# Revit family: Weitspannkabelleiter - WKL 2040_2050_2060 FT
name_source: partatom
category: Generic Models
revit_build: Autodesk Revit 2017 (Build: 20190508_0315(x64)
units: mm (PartAtom-declared; Revit-internal decimal feet)

## family parameters
Always vertical = Yes
Can host rebar = No
Cut with Voids When Loaded = No
Part Type = Normal
Room Calculation Point = No
Round Connector Dimension = Use Diameter
Shared = No
Work Plane-Based = No

## types (3) — shared parameters
Cut's number = 2
Manufacturer = OBO BETTERMANN
Material = hot dip galvanised
URL = http://www.obo-bettermann.com

## per-type parameters (varying)
| type | Cut's number 2 | GTIN | Manufacturer Art.No. | Width |
| WKL 2040 FT | 19 | 4012196614868 | 6232106 | 400 mm |
| WKL 2050 FT | 2 | 4012196614875 | 6232108 | 500 mm  [stored 1.64042 ft] |
| WKL 2060 FT | 19 | 4012196614882 | 6232110 | 600 mm  [stored 1.9685 ft] |

note: column(s) folded — value = type name in every type: Article Type

note: [stored X ft] marks values corroborated as IEEE doubles in the binary element streams (Revit-internal decimal feet)

## geometry (parser evidence)
native form markers: Sweep x3
no freeform markers — native parametric forms only
